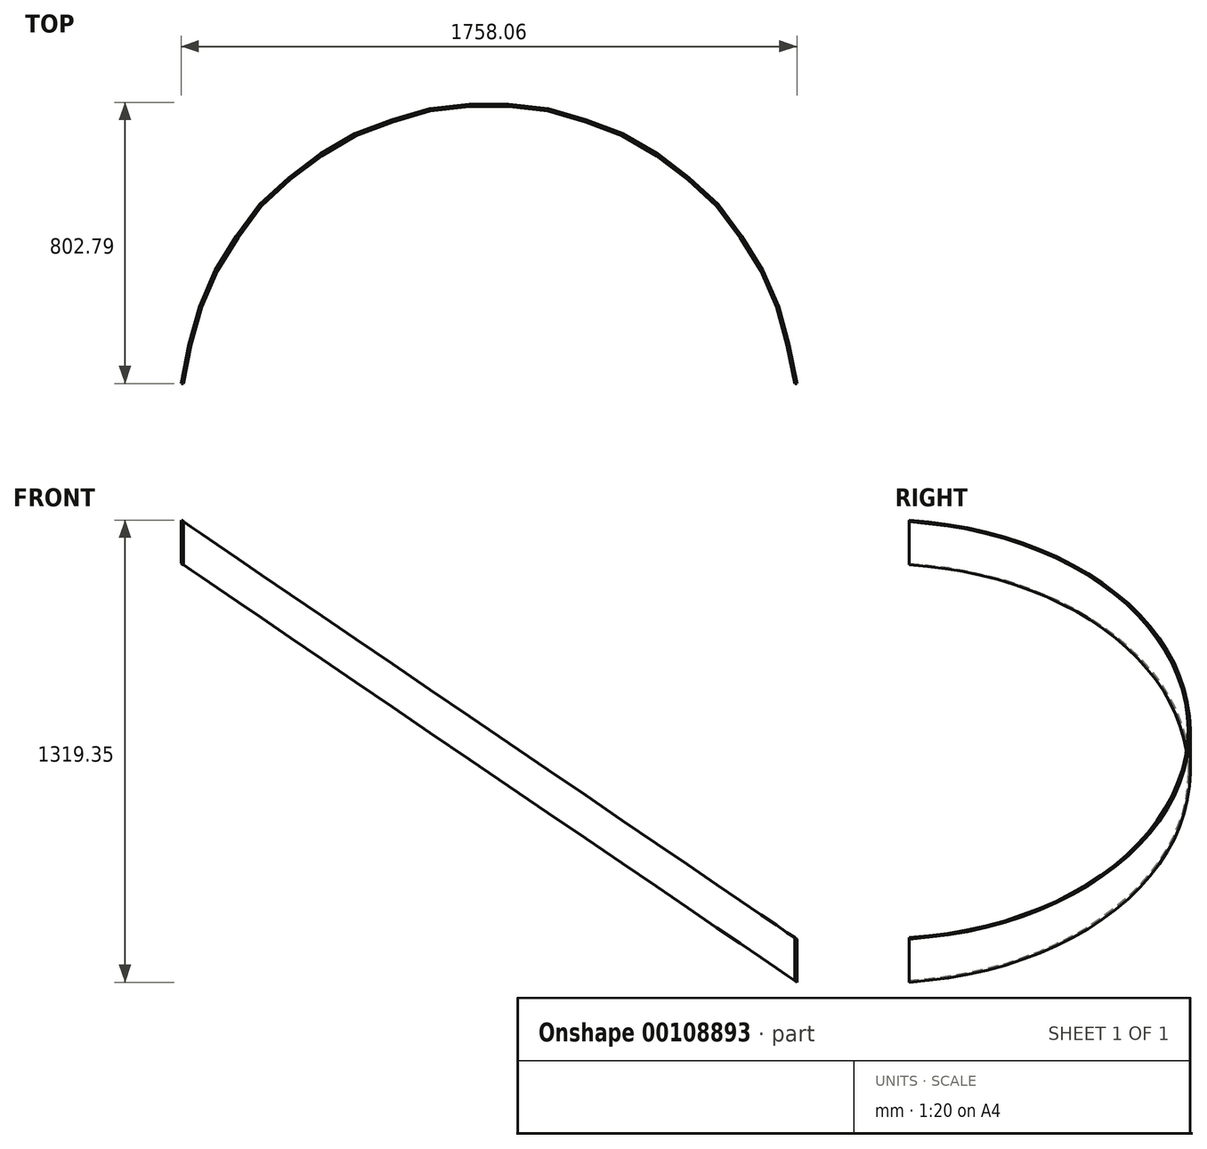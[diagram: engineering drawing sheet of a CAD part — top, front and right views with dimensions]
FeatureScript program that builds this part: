
annotation { "Feature Type Name" : "Feature", "Feature Type Description" : "" }
export const myFeature = defineFeature(function(context is Context, id is Id, definition is map)
    precondition{}
    {
        {
            var Q0;
            Q0=qCreatedBy(makeId("Top.planeOp"),FACE);
            var sketch = newSketch(context, id + "F0", { "sketchPlane" : qUnion([Q0])});
            skArc(sketch, "E0", {"start": v(879.3, 76.93) * mm, "mid": v(0, 882.65) * mm, "end": v(-879.3, 76.93) * mm});
            skArc(sketch, "E1", {"start": v(872.97, 76.37) * mm, "mid": v(0, 876.3) * mm, "end": v(-872.97, 76.37) * mm});
            skLineSegment(sketch, "E2", {"start": v(0, 0) * mm, "end": v(-879.3, 0) * mm, "construction": true});
            skLineSegment(sketch, "E3", {"start": v(0, 0) * mm, "end": v(879.3, 0) * mm, "construction": true});
            skLineSegment(sketch, "E4", {"start": v(872.97, 76.37) * mm, "end": v(879.3, 76.93) * mm});
            skLineSegment(sketch, "E5", {"start": v(-872.97, 76.37) * mm, "end": v(-872.97, 21.74) * mm});
            skLineSegment(sketch, "E6", {"start": v(-879.3, 76.93) * mm, "end": v(-879.3, 0) * mm});
            skLineSegment(sketch, "E7", {"start": v(879.3, 76.93) * mm, "end": v(879.3, 0) * mm});
            skLineSegment(sketch, "E8", {"start": v(872.97, 76.37) * mm, "end": v(872.97, 21.74) * mm});
            skLineSegment(sketch, "E9", {"start": v(-879.3, 0) * mm, "end": v(879.3, 0) * mm});
            skLineSegment(sketch, "E10.trimOffspring", {"start": v(-1022.26, 0) * mm, "end": v(-1206.82, 0) * mm, "construction": true});
            skLineSegment(sketch, "E11.trimOffspring", {"start": v(1010.53, 0) * mm, "end": v(1283.46, 0) * mm, "construction": true});
            skLineSegment(sketch, "E12", {"start": v(-872.97, 21.74) * mm, "end": v(872.97, 21.74) * mm});
            skSolve(sketch);
        }
        {
            var Q0;
            Q0 = qSketchRegion(id + "F0", true);
            extrude(context, id + "F1", {"entities" : qUnion([Q0]), "depth" : 1752.6 * mm});
        }
        {
            var Q0;
            Q0=makeQuery(id+"F1.opExtrude","SWEPT_FACE",FACE,{"disambiguationData":[OSD([sQuery(id+"F0.wireOp",EDGE,"E9")])]});
            var sketch = newSketch(context, id + "F2", { "sketchPlane" : qUnion([Q0])});
            skLineSegment(sketch, "E13", {"start": v(-914.4, 1549.4) * mm, "end": v(914.4, 304.8) * mm});
            skLineSegment(sketch, "E14", {"start": v(-914.4, 1549.4) * mm, "end": v(-914.4, 1821.49) * mm});
            skLineSegment(sketch, "E15", {"start": v(-914.4, 1821.49) * mm, "end": v(994.87, 1821.49) * mm});
            skLineSegment(sketch, "E16", {"start": v(994.87, 1821.49) * mm, "end": v(914.4, 304.8) * mm});
            skSolve(sketch);
        }
        {
            var Q0;
            Q0 = qSketchRegion(id + "F2", true);
            extrude(context, id + "F3", {"entities" : qUnion([Q0]), "operationType" : NewBodyOperationType.REMOVE, "endBound" : BoundingType.THROUGH_ALL, "oppositeDirection" : true, "depth" : 25.4 * mm});
        }
        {
            var Q0;
            Q0=makeQuery(id+"F1.opExtrude","SWEPT_FACE",FACE,{"disambiguationData":[OSD([sQuery(id+"F0.wireOp",EDGE,"E9")])]});
            var sketch = newSketch(context, id + "F4", { "sketchPlane" : qUnion([Q0])});
            skLineSegment(sketch, "E17", {"start": v(-914.4, 1426.5) * mm, "end": v(-914.4, 0) * mm});
            skLineSegment(sketch, "E18", {"start": v(914.4, 181.9) * mm, "end": v(914.4, 0) * mm});
            skLineSegment(sketch, "E19", {"start": v(-914.4, 0) * mm, "end": v(914.4, 0) * mm});
            skPoint(sketch, "E20.orphan", {"position": v(-1172.24, 0) * mm});
            skLineSegment(sketch, "E21", {"start": v(-914.4, 1426.5) * mm, "end": v(857.24, 220.8) * mm});
            skLineSegment(sketch, "E22", {"start": v(857.24, 220.8) * mm, "end": v(914.4, 181.9) * mm});
            skSolve(sketch);
        }
        {
            var Q0;
            Q0=qCreatedBy(makeId("Top.planeOp"),FACE);
            var sketch = newSketch(context, id + "F5", { "sketchPlane" : qUnion([Q0])});
            skLineSegment(sketch, "E23", {"start": v(-1011.6, 0) * mm, "end": v(1011.6, 0) * mm});
            skLineSegment(sketch, "E24", {"start": v(-1011.6, 0) * mm, "end": v(-1011.6, 79.86) * mm});
            skLineSegment(sketch, "E25", {"start": v(-1011.6, 79.86) * mm, "end": v(1018.67, 79.86) * mm});
            skLineSegment(sketch, "E26", {"start": v(1018.67, 79.86) * mm, "end": v(1011.6, 0) * mm});
            skSolve(sketch);
        }
        {
            var Q0;
            Q0 = qSketchRegion(id + "F4", true);
            extrude(context, id + "F6", {"entities" : qUnion([Q0]), "operationType" : NewBodyOperationType.REMOVE, "endBound" : BoundingType.THROUGH_ALL, "oppositeDirection" : true, "depth" : 25.4 * mm});
        }
        {
            var Q0;
            Q0 = qSketchRegion(id + "F5", true);
            extrude(context, id + "F7", {"entities" : qUnion([Q0]), "operationType" : NewBodyOperationType.REMOVE, "endBound" : BoundingType.THROUGH_ALL, "depth" : 25.4 * mm});
        }
    });
